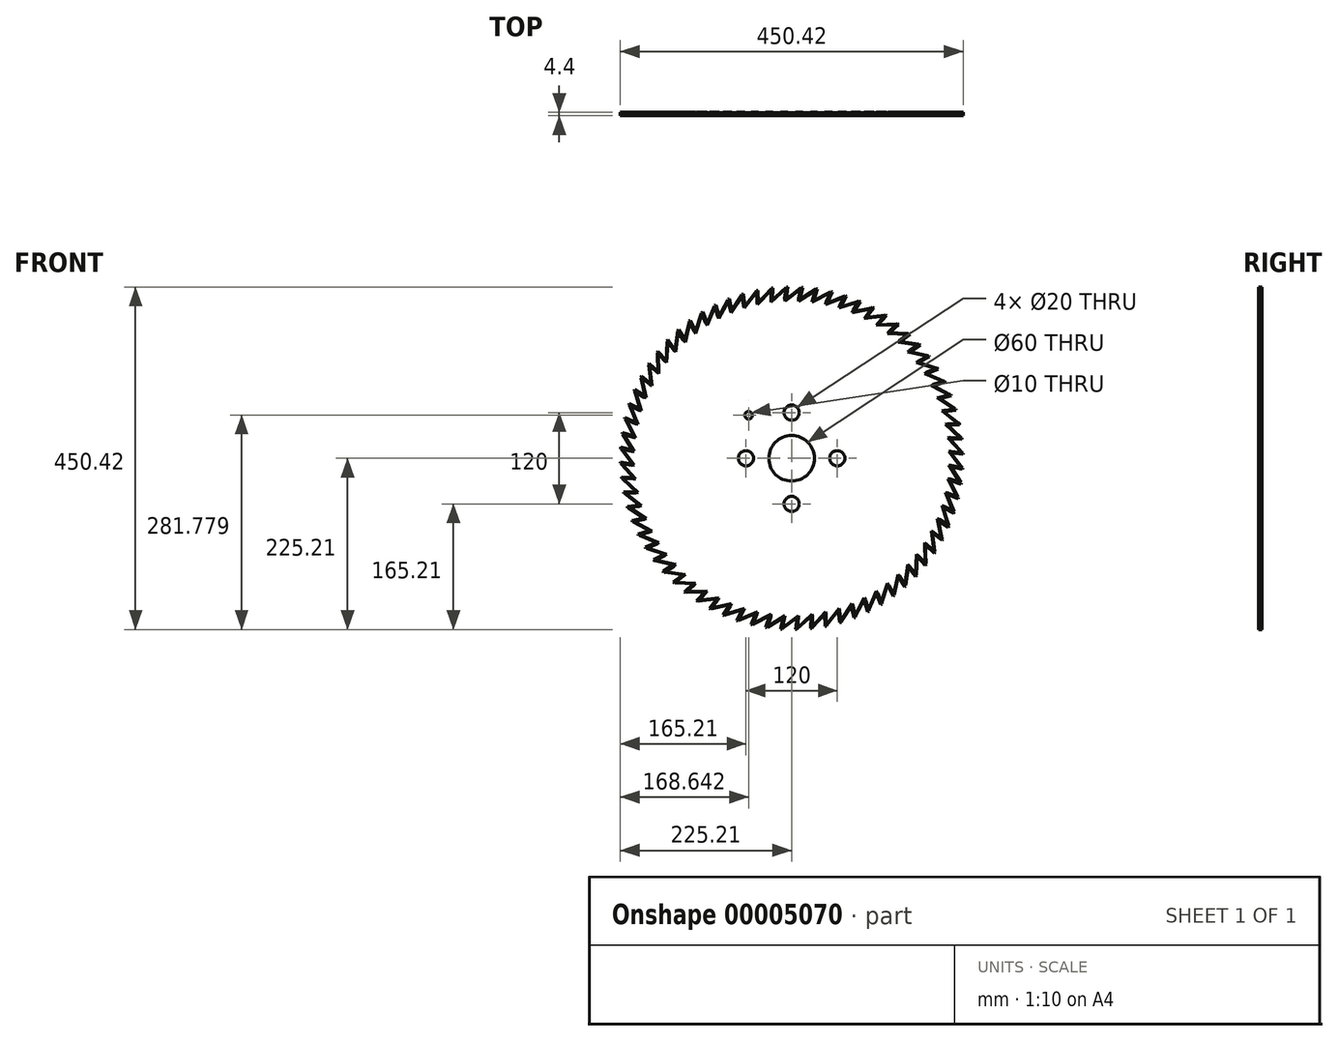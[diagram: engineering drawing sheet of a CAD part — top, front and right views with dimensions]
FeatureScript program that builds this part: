
annotation { "Feature Type Name" : "Feature", "Feature Type Description" : "" }
export const myFeature = defineFeature(function(context is Context, id is Id, definition is map)
    precondition{}
    {
        {
            var Q0;
            Q0=qCreatedBy(makeId("Right.planeOp"),FACE);
            var sketch = newSketch(context, id + "F0", { "sketchPlane" : qUnion([Q0])});
            skLineSegment(sketch, "E0", {"start": v(-63.93, 0) * mm, "end": v(105.28, 0) * mm, "construction": true});
            skSolve(sketch);
        }
        {
            var Q0;
            Q0=qCreatedBy(makeId("Front.planeOp"),FACE);
            var sketch = newSketch(context, id + "F1", { "sketchPlane" : qUnion([Q0])});
            skLineSegment(sketch, "E1", {"start": v(0, 0) * mm, "end": v(-1.3, 29.97) * mm, "construction": true});
            skLineSegment(sketch, "E2", {"start": v(-9.08, 208) * mm, "end": v(12.27, 224) * mm});
            skLineSegment(sketch, "E3", {"start": v(12.27, 224) * mm, "end": v(9.17, 210) * mm});
            skLineSegment(sketch, "E4", {"start": v(9.17, 210) * mm, "end": v(1.3, 29.97) * mm});
            skLineSegment(sketch, "E5", {"start": v(-1.3, 29.97) * mm, "end": v(-9.08, 208) * mm});
            skLineSegment(sketch, "E6", {"start": v(1.3, 29.97) * mm, "end": v(0, 0) * mm, "construction": true});
            skArc(sketch, "E7", {"start": v(1.3, 29.97) * mm, "mid": v(0, 30) * mm, "end": v(-1.3, 29.97) * mm});
            skArc(sketch, "E8", {"start": v(-1.3, 29.97) * mm, "mid": v(0, -30) * mm, "end": v(1.3, 29.97) * mm, "construction": true});
            skSolve(sketch);
        }
        {
            var Q0;
            Q0=qSketchRegion(id+"F1",true);
            extrude(context, id + "F2", {"entities" : qUnion([Q0]), "depth" : 4 * mm});
        }
        {
            var Q0;
            Q0=makeQuery(id+"F2.opExtrude","CAP_EDGE",EDGE,{"disambiguationData":[OSD([sQuery(id+"F1.wireOp",EDGE,"E2")])],"isStart":true});
            var Q1;
            Q1=makeQuery(id+"F2.opExtrude","CAP_EDGE",EDGE,{"disambiguationData":[OSD([sQuery(id+"F1.wireOp",EDGE,"E2")])],"isStart":false});
            chamfer(context, id + "F3", {"entities" : qUnion([Q0, Q1]), "width" : 1 * mm, "tangentPropagation" : true});
        }
        {
            var Q0;
            Q0=makeQuery(id+"F2.opExtrude","CAP_FACE",FACE,{"disambiguationData":[OSD([sQuery(id+"F1.wireOp",EDGE,"E2"),sQuery(id+"F1.wireOp",EDGE,"E3"),sQuery(id+"F1.wireOp",EDGE,"E4"),sQuery(id+"F1.wireOp",EDGE,"E5"),sQuery(id+"F1.wireOp",EDGE,"E7")])],"isStart":false});
            var Q1;
            Q1=makeQuery(id+"F2.opExtrude","SWEPT_FACE",FACE,{"disambiguationData":[OSD([sQuery(id+"F1.wireOp",EDGE,"E4")])]});
            var Q2;
            Q2=makeQuery(id+"F2.opExtrude","SWEPT_FACE",FACE,{"disambiguationData":[OSD([sQuery(id+"F1.wireOp",EDGE,"E3")])]});
            var Q3;
            Q3=makeQuery(id+"F2.opExtrude","SWEPT_FACE",FACE,{"disambiguationData":[OSD([sQuery(id+"F1.wireOp",EDGE,"E2")])]});
            var Q4;
            Q4=makeQuery(id+"F2.opExtrude","SWEPT_FACE",FACE,{"disambiguationData":[OSD([sQuery(id+"F1.wireOp",EDGE,"E5")])]});
            var Q5;
            Q5=makeQuery(id+"F2.opExtrude","CAP_FACE",FACE,{"disambiguationData":[OSD([sQuery(id+"F1.wireOp",EDGE,"E2"),sQuery(id+"F1.wireOp",EDGE,"E3"),sQuery(id+"F1.wireOp",EDGE,"E4"),sQuery(id+"F1.wireOp",EDGE,"E5"),sQuery(id+"F1.wireOp",EDGE,"E7")])],"isStart":true});
            var Q6;
            Q6=makeQuery(id+"F2.opExtrude","SWEPT_FACE",FACE,{"disambiguationData":[OSD([sQuery(id+"F1.wireOp",EDGE,"E7")])]});
            var Q7;
            {var subQ0=sQuery(id+"F1.wireOp",EDGE,"E2");Q7=makeQuery(id+"F3.opChamfer","BLEND_FACE",FACE,{"disambiguationData":[OSD([subQ0]),TDD([makeQuery(id+"F2.opExtrude","CAP_EDGE",EDGE,{"disambiguationData":[OSD([subQ0])],"isStart":false})])]});}
            var Q8;
            {var subQ0=sQuery(id+"F1.wireOp",EDGE,"E2");Q8=makeQuery(id+"F3.opChamfer","BLEND_FACE",FACE,{"disambiguationData":[OSD([subQ0]),TDD([makeQuery(id+"F2.opExtrude","CAP_EDGE",EDGE,{"disambiguationData":[OSD([subQ0])],"isStart":true})])]});}
            var Q9;
            Q9=makeQuery(id+"F2.opExtrude","SWEPT_BODY",BODY,{"disambiguationData":[OSD([sQuery(id+"F1.wireOp",EDGE,"E2"),sQuery(id+"F1.wireOp",EDGE,"E3"),sQuery(id+"F1.wireOp",EDGE,"E4"),sQuery(id+"F1.wireOp",EDGE,"E5"),sQuery(id+"F1.wireOp",EDGE,"E7")])]});
            var Q10;
            Q10=sQuery(id+"F0.wireOp",EDGE,"E0");
            circularPattern(context, id + "F4", {"faces" : qUnion([Q0, Q1, Q2, Q3, Q4, Q5, Q6, Q7, Q8]), "axis" : qUnion([Q10]), "angle" : 5 * degree, "instanceCount" : round(72), "patternType" : PatternType.FACE});
        }
        {
            var Q0;
            Q0=makeQuery(id+"F2.opExtrude","SWEPT_BODY",BODY,{"disambiguationData":[OSD([sQuery(id+"F1.wireOp",EDGE,"E2"),sQuery(id+"F1.wireOp",EDGE,"E3"),sQuery(id+"F1.wireOp",EDGE,"E4"),sQuery(id+"F1.wireOp",EDGE,"E5"),sQuery(id+"F1.wireOp",EDGE,"E7")])]});
            var Q1;
            Q1=makeQuery(id+"F4.opPattern","COPY",BODY,{"derivedFrom":makeQuery(id+"F2.opExtrude","SWEPT_BODY",BODY,{"disambiguationData":[OSD([sQuery(id+"F1.wireOp",EDGE,"E2"),sQuery(id+"F1.wireOp",EDGE,"E3"),sQuery(id+"F1.wireOp",EDGE,"E4"),sQuery(id+"F1.wireOp",EDGE,"E5"),sQuery(id+"F1.wireOp",EDGE,"E7")])]}),"instanceName":"1"});
            var Q2;
            Q2=makeQuery(id+"F4.opPattern","COPY",BODY,{"derivedFrom":makeQuery(id+"F2.opExtrude","SWEPT_BODY",BODY,{"disambiguationData":[OSD([sQuery(id+"F1.wireOp",EDGE,"E2"),sQuery(id+"F1.wireOp",EDGE,"E3"),sQuery(id+"F1.wireOp",EDGE,"E4"),sQuery(id+"F1.wireOp",EDGE,"E5"),sQuery(id+"F1.wireOp",EDGE,"E7")])]}),"instanceName":"2"});
            var Q3;
            Q3=makeQuery(id+"F4.opPattern","COPY",BODY,{"derivedFrom":makeQuery(id+"F2.opExtrude","SWEPT_BODY",BODY,{"disambiguationData":[OSD([sQuery(id+"F1.wireOp",EDGE,"E2"),sQuery(id+"F1.wireOp",EDGE,"E3"),sQuery(id+"F1.wireOp",EDGE,"E4"),sQuery(id+"F1.wireOp",EDGE,"E5"),sQuery(id+"F1.wireOp",EDGE,"E7")])]}),"instanceName":"3"});
            var Q4;
            Q4=makeQuery(id+"F4.opPattern","COPY",BODY,{"derivedFrom":makeQuery(id+"F2.opExtrude","SWEPT_BODY",BODY,{"disambiguationData":[OSD([sQuery(id+"F1.wireOp",EDGE,"E2"),sQuery(id+"F1.wireOp",EDGE,"E3"),sQuery(id+"F1.wireOp",EDGE,"E4"),sQuery(id+"F1.wireOp",EDGE,"E5"),sQuery(id+"F1.wireOp",EDGE,"E7")])]}),"instanceName":"4"});
            var Q5;
            Q5=makeQuery(id+"F4.opPattern","COPY",BODY,{"derivedFrom":makeQuery(id+"F2.opExtrude","SWEPT_BODY",BODY,{"disambiguationData":[OSD([sQuery(id+"F1.wireOp",EDGE,"E2"),sQuery(id+"F1.wireOp",EDGE,"E3"),sQuery(id+"F1.wireOp",EDGE,"E4"),sQuery(id+"F1.wireOp",EDGE,"E5"),sQuery(id+"F1.wireOp",EDGE,"E7")])]}),"instanceName":"5"});
            var Q6;
            Q6=makeQuery(id+"F4.opPattern","COPY",BODY,{"derivedFrom":makeQuery(id+"F2.opExtrude","SWEPT_BODY",BODY,{"disambiguationData":[OSD([sQuery(id+"F1.wireOp",EDGE,"E2"),sQuery(id+"F1.wireOp",EDGE,"E3"),sQuery(id+"F1.wireOp",EDGE,"E4"),sQuery(id+"F1.wireOp",EDGE,"E5"),sQuery(id+"F1.wireOp",EDGE,"E7")])]}),"instanceName":"6"});
            var Q7;
            Q7=makeQuery(id+"F4.opPattern","COPY",BODY,{"derivedFrom":makeQuery(id+"F2.opExtrude","SWEPT_BODY",BODY,{"disambiguationData":[OSD([sQuery(id+"F1.wireOp",EDGE,"E2"),sQuery(id+"F1.wireOp",EDGE,"E3"),sQuery(id+"F1.wireOp",EDGE,"E4"),sQuery(id+"F1.wireOp",EDGE,"E5"),sQuery(id+"F1.wireOp",EDGE,"E7")])]}),"instanceName":"7"});
            var Q8;
            Q8=makeQuery(id+"F4.opPattern","COPY",BODY,{"derivedFrom":makeQuery(id+"F2.opExtrude","SWEPT_BODY",BODY,{"disambiguationData":[OSD([sQuery(id+"F1.wireOp",EDGE,"E2"),sQuery(id+"F1.wireOp",EDGE,"E3"),sQuery(id+"F1.wireOp",EDGE,"E4"),sQuery(id+"F1.wireOp",EDGE,"E5"),sQuery(id+"F1.wireOp",EDGE,"E7")])]}),"instanceName":"8"});
            var Q9;
            Q9=makeQuery(id+"F4.opPattern","COPY",BODY,{"derivedFrom":makeQuery(id+"F2.opExtrude","SWEPT_BODY",BODY,{"disambiguationData":[OSD([sQuery(id+"F1.wireOp",EDGE,"E2"),sQuery(id+"F1.wireOp",EDGE,"E3"),sQuery(id+"F1.wireOp",EDGE,"E4"),sQuery(id+"F1.wireOp",EDGE,"E5"),sQuery(id+"F1.wireOp",EDGE,"E7")])]}),"instanceName":"9"});
            var Q10;
            Q10=makeQuery(id+"F4.opPattern","COPY",BODY,{"derivedFrom":makeQuery(id+"F2.opExtrude","SWEPT_BODY",BODY,{"disambiguationData":[OSD([sQuery(id+"F1.wireOp",EDGE,"E2"),sQuery(id+"F1.wireOp",EDGE,"E3"),sQuery(id+"F1.wireOp",EDGE,"E4"),sQuery(id+"F1.wireOp",EDGE,"E5"),sQuery(id+"F1.wireOp",EDGE,"E7")])]}),"instanceName":"10"});
            var Q11;
            Q11=makeQuery(id+"F4.opPattern","COPY",BODY,{"derivedFrom":makeQuery(id+"F2.opExtrude","SWEPT_BODY",BODY,{"disambiguationData":[OSD([sQuery(id+"F1.wireOp",EDGE,"E2"),sQuery(id+"F1.wireOp",EDGE,"E3"),sQuery(id+"F1.wireOp",EDGE,"E4"),sQuery(id+"F1.wireOp",EDGE,"E5"),sQuery(id+"F1.wireOp",EDGE,"E7")])]}),"instanceName":"11"});
            var Q12;
            Q12=makeQuery(id+"F4.opPattern","COPY",BODY,{"derivedFrom":makeQuery(id+"F2.opExtrude","SWEPT_BODY",BODY,{"disambiguationData":[OSD([sQuery(id+"F1.wireOp",EDGE,"E2"),sQuery(id+"F1.wireOp",EDGE,"E3"),sQuery(id+"F1.wireOp",EDGE,"E4"),sQuery(id+"F1.wireOp",EDGE,"E5"),sQuery(id+"F1.wireOp",EDGE,"E7")])]}),"instanceName":"12"});
            var Q13;
            Q13=makeQuery(id+"F4.opPattern","COPY",BODY,{"derivedFrom":makeQuery(id+"F2.opExtrude","SWEPT_BODY",BODY,{"disambiguationData":[OSD([sQuery(id+"F1.wireOp",EDGE,"E2"),sQuery(id+"F1.wireOp",EDGE,"E3"),sQuery(id+"F1.wireOp",EDGE,"E4"),sQuery(id+"F1.wireOp",EDGE,"E5"),sQuery(id+"F1.wireOp",EDGE,"E7")])]}),"instanceName":"13"});
            var Q14;
            Q14=makeQuery(id+"F4.opPattern","COPY",BODY,{"derivedFrom":makeQuery(id+"F2.opExtrude","SWEPT_BODY",BODY,{"disambiguationData":[OSD([sQuery(id+"F1.wireOp",EDGE,"E2"),sQuery(id+"F1.wireOp",EDGE,"E3"),sQuery(id+"F1.wireOp",EDGE,"E4"),sQuery(id+"F1.wireOp",EDGE,"E5"),sQuery(id+"F1.wireOp",EDGE,"E7")])]}),"instanceName":"14"});
            var Q15;
            Q15=makeQuery(id+"F4.opPattern","COPY",BODY,{"derivedFrom":makeQuery(id+"F2.opExtrude","SWEPT_BODY",BODY,{"disambiguationData":[OSD([sQuery(id+"F1.wireOp",EDGE,"E2"),sQuery(id+"F1.wireOp",EDGE,"E3"),sQuery(id+"F1.wireOp",EDGE,"E4"),sQuery(id+"F1.wireOp",EDGE,"E5"),sQuery(id+"F1.wireOp",EDGE,"E7")])]}),"instanceName":"15"});
            var Q16;
            Q16=makeQuery(id+"F4.opPattern","COPY",BODY,{"derivedFrom":makeQuery(id+"F2.opExtrude","SWEPT_BODY",BODY,{"disambiguationData":[OSD([sQuery(id+"F1.wireOp",EDGE,"E2"),sQuery(id+"F1.wireOp",EDGE,"E3"),sQuery(id+"F1.wireOp",EDGE,"E4"),sQuery(id+"F1.wireOp",EDGE,"E5"),sQuery(id+"F1.wireOp",EDGE,"E7")])]}),"instanceName":"16"});
            var Q17;
            Q17=makeQuery(id+"F4.opPattern","COPY",BODY,{"derivedFrom":makeQuery(id+"F2.opExtrude","SWEPT_BODY",BODY,{"disambiguationData":[OSD([sQuery(id+"F1.wireOp",EDGE,"E2"),sQuery(id+"F1.wireOp",EDGE,"E3"),sQuery(id+"F1.wireOp",EDGE,"E4"),sQuery(id+"F1.wireOp",EDGE,"E5"),sQuery(id+"F1.wireOp",EDGE,"E7")])]}),"instanceName":"17"});
            var Q18;
            Q18=makeQuery(id+"F4.opPattern","COPY",BODY,{"derivedFrom":makeQuery(id+"F2.opExtrude","SWEPT_BODY",BODY,{"disambiguationData":[OSD([sQuery(id+"F1.wireOp",EDGE,"E2"),sQuery(id+"F1.wireOp",EDGE,"E3"),sQuery(id+"F1.wireOp",EDGE,"E4"),sQuery(id+"F1.wireOp",EDGE,"E5"),sQuery(id+"F1.wireOp",EDGE,"E7")])]}),"instanceName":"18"});
            var Q19;
            Q19=makeQuery(id+"F4.opPattern","COPY",BODY,{"derivedFrom":makeQuery(id+"F2.opExtrude","SWEPT_BODY",BODY,{"disambiguationData":[OSD([sQuery(id+"F1.wireOp",EDGE,"E2"),sQuery(id+"F1.wireOp",EDGE,"E3"),sQuery(id+"F1.wireOp",EDGE,"E4"),sQuery(id+"F1.wireOp",EDGE,"E5"),sQuery(id+"F1.wireOp",EDGE,"E7")])]}),"instanceName":"19"});
            var Q20;
            Q20=makeQuery(id+"F4.opPattern","COPY",BODY,{"derivedFrom":makeQuery(id+"F2.opExtrude","SWEPT_BODY",BODY,{"disambiguationData":[OSD([sQuery(id+"F1.wireOp",EDGE,"E2"),sQuery(id+"F1.wireOp",EDGE,"E3"),sQuery(id+"F1.wireOp",EDGE,"E4"),sQuery(id+"F1.wireOp",EDGE,"E5"),sQuery(id+"F1.wireOp",EDGE,"E7")])]}),"instanceName":"20"});
            var Q21;
            Q21=makeQuery(id+"F4.opPattern","COPY",BODY,{"derivedFrom":makeQuery(id+"F2.opExtrude","SWEPT_BODY",BODY,{"disambiguationData":[OSD([sQuery(id+"F1.wireOp",EDGE,"E2"),sQuery(id+"F1.wireOp",EDGE,"E3"),sQuery(id+"F1.wireOp",EDGE,"E4"),sQuery(id+"F1.wireOp",EDGE,"E5"),sQuery(id+"F1.wireOp",EDGE,"E7")])]}),"instanceName":"21"});
            var Q22;
            Q22=makeQuery(id+"F4.opPattern","COPY",BODY,{"derivedFrom":makeQuery(id+"F2.opExtrude","SWEPT_BODY",BODY,{"disambiguationData":[OSD([sQuery(id+"F1.wireOp",EDGE,"E2"),sQuery(id+"F1.wireOp",EDGE,"E3"),sQuery(id+"F1.wireOp",EDGE,"E4"),sQuery(id+"F1.wireOp",EDGE,"E5"),sQuery(id+"F1.wireOp",EDGE,"E7")])]}),"instanceName":"22"});
            var Q23;
            Q23=makeQuery(id+"F4.opPattern","COPY",BODY,{"derivedFrom":makeQuery(id+"F2.opExtrude","SWEPT_BODY",BODY,{"disambiguationData":[OSD([sQuery(id+"F1.wireOp",EDGE,"E2"),sQuery(id+"F1.wireOp",EDGE,"E3"),sQuery(id+"F1.wireOp",EDGE,"E4"),sQuery(id+"F1.wireOp",EDGE,"E5"),sQuery(id+"F1.wireOp",EDGE,"E7")])]}),"instanceName":"23"});
            var Q24;
            Q24=makeQuery(id+"F4.opPattern","COPY",BODY,{"derivedFrom":makeQuery(id+"F2.opExtrude","SWEPT_BODY",BODY,{"disambiguationData":[OSD([sQuery(id+"F1.wireOp",EDGE,"E2"),sQuery(id+"F1.wireOp",EDGE,"E3"),sQuery(id+"F1.wireOp",EDGE,"E4"),sQuery(id+"F1.wireOp",EDGE,"E5"),sQuery(id+"F1.wireOp",EDGE,"E7")])]}),"instanceName":"24"});
            var Q25;
            Q25=makeQuery(id+"F4.opPattern","COPY",BODY,{"derivedFrom":makeQuery(id+"F2.opExtrude","SWEPT_BODY",BODY,{"disambiguationData":[OSD([sQuery(id+"F1.wireOp",EDGE,"E2"),sQuery(id+"F1.wireOp",EDGE,"E3"),sQuery(id+"F1.wireOp",EDGE,"E4"),sQuery(id+"F1.wireOp",EDGE,"E5"),sQuery(id+"F1.wireOp",EDGE,"E7")])]}),"instanceName":"25"});
            var Q26;
            Q26=makeQuery(id+"F4.opPattern","COPY",BODY,{"derivedFrom":makeQuery(id+"F2.opExtrude","SWEPT_BODY",BODY,{"disambiguationData":[OSD([sQuery(id+"F1.wireOp",EDGE,"E2"),sQuery(id+"F1.wireOp",EDGE,"E3"),sQuery(id+"F1.wireOp",EDGE,"E4"),sQuery(id+"F1.wireOp",EDGE,"E5"),sQuery(id+"F1.wireOp",EDGE,"E7")])]}),"instanceName":"26"});
            var Q27;
            Q27=makeQuery(id+"F4.opPattern","COPY",BODY,{"derivedFrom":makeQuery(id+"F2.opExtrude","SWEPT_BODY",BODY,{"disambiguationData":[OSD([sQuery(id+"F1.wireOp",EDGE,"E2"),sQuery(id+"F1.wireOp",EDGE,"E3"),sQuery(id+"F1.wireOp",EDGE,"E4"),sQuery(id+"F1.wireOp",EDGE,"E5"),sQuery(id+"F1.wireOp",EDGE,"E7")])]}),"instanceName":"27"});
            var Q28;
            Q28=makeQuery(id+"F4.opPattern","COPY",BODY,{"derivedFrom":makeQuery(id+"F2.opExtrude","SWEPT_BODY",BODY,{"disambiguationData":[OSD([sQuery(id+"F1.wireOp",EDGE,"E2"),sQuery(id+"F1.wireOp",EDGE,"E3"),sQuery(id+"F1.wireOp",EDGE,"E4"),sQuery(id+"F1.wireOp",EDGE,"E5"),sQuery(id+"F1.wireOp",EDGE,"E7")])]}),"instanceName":"28"});
            var Q29;
            Q29=makeQuery(id+"F4.opPattern","COPY",BODY,{"derivedFrom":makeQuery(id+"F2.opExtrude","SWEPT_BODY",BODY,{"disambiguationData":[OSD([sQuery(id+"F1.wireOp",EDGE,"E2"),sQuery(id+"F1.wireOp",EDGE,"E3"),sQuery(id+"F1.wireOp",EDGE,"E4"),sQuery(id+"F1.wireOp",EDGE,"E5"),sQuery(id+"F1.wireOp",EDGE,"E7")])]}),"instanceName":"29"});
            var Q30;
            Q30=makeQuery(id+"F4.opPattern","COPY",BODY,{"derivedFrom":makeQuery(id+"F2.opExtrude","SWEPT_BODY",BODY,{"disambiguationData":[OSD([sQuery(id+"F1.wireOp",EDGE,"E2"),sQuery(id+"F1.wireOp",EDGE,"E3"),sQuery(id+"F1.wireOp",EDGE,"E4"),sQuery(id+"F1.wireOp",EDGE,"E5"),sQuery(id+"F1.wireOp",EDGE,"E7")])]}),"instanceName":"30"});
            var Q31;
            Q31=makeQuery(id+"F4.opPattern","COPY",BODY,{"derivedFrom":makeQuery(id+"F2.opExtrude","SWEPT_BODY",BODY,{"disambiguationData":[OSD([sQuery(id+"F1.wireOp",EDGE,"E2"),sQuery(id+"F1.wireOp",EDGE,"E3"),sQuery(id+"F1.wireOp",EDGE,"E4"),sQuery(id+"F1.wireOp",EDGE,"E5"),sQuery(id+"F1.wireOp",EDGE,"E7")])]}),"instanceName":"31"});
            var Q32;
            Q32=makeQuery(id+"F4.opPattern","COPY",BODY,{"derivedFrom":makeQuery(id+"F2.opExtrude","SWEPT_BODY",BODY,{"disambiguationData":[OSD([sQuery(id+"F1.wireOp",EDGE,"E2"),sQuery(id+"F1.wireOp",EDGE,"E3"),sQuery(id+"F1.wireOp",EDGE,"E4"),sQuery(id+"F1.wireOp",EDGE,"E5"),sQuery(id+"F1.wireOp",EDGE,"E7")])]}),"instanceName":"32"});
            var Q33;
            Q33=makeQuery(id+"F4.opPattern","COPY",BODY,{"derivedFrom":makeQuery(id+"F2.opExtrude","SWEPT_BODY",BODY,{"disambiguationData":[OSD([sQuery(id+"F1.wireOp",EDGE,"E2"),sQuery(id+"F1.wireOp",EDGE,"E3"),sQuery(id+"F1.wireOp",EDGE,"E4"),sQuery(id+"F1.wireOp",EDGE,"E5"),sQuery(id+"F1.wireOp",EDGE,"E7")])]}),"instanceName":"33"});
            var Q34;
            Q34=makeQuery(id+"F4.opPattern","COPY",BODY,{"derivedFrom":makeQuery(id+"F2.opExtrude","SWEPT_BODY",BODY,{"disambiguationData":[OSD([sQuery(id+"F1.wireOp",EDGE,"E2"),sQuery(id+"F1.wireOp",EDGE,"E3"),sQuery(id+"F1.wireOp",EDGE,"E4"),sQuery(id+"F1.wireOp",EDGE,"E5"),sQuery(id+"F1.wireOp",EDGE,"E7")])]}),"instanceName":"34"});
            var Q35;
            Q35=makeQuery(id+"F4.opPattern","COPY",BODY,{"derivedFrom":makeQuery(id+"F2.opExtrude","SWEPT_BODY",BODY,{"disambiguationData":[OSD([sQuery(id+"F1.wireOp",EDGE,"E2"),sQuery(id+"F1.wireOp",EDGE,"E3"),sQuery(id+"F1.wireOp",EDGE,"E4"),sQuery(id+"F1.wireOp",EDGE,"E5"),sQuery(id+"F1.wireOp",EDGE,"E7")])]}),"instanceName":"35"});
            var Q36;
            Q36=makeQuery(id+"F4.opPattern","COPY",BODY,{"derivedFrom":makeQuery(id+"F2.opExtrude","SWEPT_BODY",BODY,{"disambiguationData":[OSD([sQuery(id+"F1.wireOp",EDGE,"E2"),sQuery(id+"F1.wireOp",EDGE,"E3"),sQuery(id+"F1.wireOp",EDGE,"E4"),sQuery(id+"F1.wireOp",EDGE,"E5"),sQuery(id+"F1.wireOp",EDGE,"E7")])]}),"instanceName":"36"});
            var Q37;
            Q37=makeQuery(id+"F4.opPattern","COPY",BODY,{"derivedFrom":makeQuery(id+"F2.opExtrude","SWEPT_BODY",BODY,{"disambiguationData":[OSD([sQuery(id+"F1.wireOp",EDGE,"E2"),sQuery(id+"F1.wireOp",EDGE,"E3"),sQuery(id+"F1.wireOp",EDGE,"E4"),sQuery(id+"F1.wireOp",EDGE,"E5"),sQuery(id+"F1.wireOp",EDGE,"E7")])]}),"instanceName":"37"});
            var Q38;
            Q38=makeQuery(id+"F4.opPattern","COPY",BODY,{"derivedFrom":makeQuery(id+"F2.opExtrude","SWEPT_BODY",BODY,{"disambiguationData":[OSD([sQuery(id+"F1.wireOp",EDGE,"E2"),sQuery(id+"F1.wireOp",EDGE,"E3"),sQuery(id+"F1.wireOp",EDGE,"E4"),sQuery(id+"F1.wireOp",EDGE,"E5"),sQuery(id+"F1.wireOp",EDGE,"E7")])]}),"instanceName":"38"});
            var Q39;
            Q39=makeQuery(id+"F4.opPattern","COPY",BODY,{"derivedFrom":makeQuery(id+"F2.opExtrude","SWEPT_BODY",BODY,{"disambiguationData":[OSD([sQuery(id+"F1.wireOp",EDGE,"E2"),sQuery(id+"F1.wireOp",EDGE,"E3"),sQuery(id+"F1.wireOp",EDGE,"E4"),sQuery(id+"F1.wireOp",EDGE,"E5"),sQuery(id+"F1.wireOp",EDGE,"E7")])]}),"instanceName":"39"});
            var Q40;
            Q40=makeQuery(id+"F4.opPattern","COPY",BODY,{"derivedFrom":makeQuery(id+"F2.opExtrude","SWEPT_BODY",BODY,{"disambiguationData":[OSD([sQuery(id+"F1.wireOp",EDGE,"E2"),sQuery(id+"F1.wireOp",EDGE,"E3"),sQuery(id+"F1.wireOp",EDGE,"E4"),sQuery(id+"F1.wireOp",EDGE,"E5"),sQuery(id+"F1.wireOp",EDGE,"E7")])]}),"instanceName":"40"});
            var Q41;
            Q41=makeQuery(id+"F4.opPattern","COPY",BODY,{"derivedFrom":makeQuery(id+"F2.opExtrude","SWEPT_BODY",BODY,{"disambiguationData":[OSD([sQuery(id+"F1.wireOp",EDGE,"E2"),sQuery(id+"F1.wireOp",EDGE,"E3"),sQuery(id+"F1.wireOp",EDGE,"E4"),sQuery(id+"F1.wireOp",EDGE,"E5"),sQuery(id+"F1.wireOp",EDGE,"E7")])]}),"instanceName":"41"});
            var Q42;
            Q42=makeQuery(id+"F4.opPattern","COPY",BODY,{"derivedFrom":makeQuery(id+"F2.opExtrude","SWEPT_BODY",BODY,{"disambiguationData":[OSD([sQuery(id+"F1.wireOp",EDGE,"E2"),sQuery(id+"F1.wireOp",EDGE,"E3"),sQuery(id+"F1.wireOp",EDGE,"E4"),sQuery(id+"F1.wireOp",EDGE,"E5"),sQuery(id+"F1.wireOp",EDGE,"E7")])]}),"instanceName":"42"});
            var Q43;
            Q43=makeQuery(id+"F4.opPattern","COPY",BODY,{"derivedFrom":makeQuery(id+"F2.opExtrude","SWEPT_BODY",BODY,{"disambiguationData":[OSD([sQuery(id+"F1.wireOp",EDGE,"E2"),sQuery(id+"F1.wireOp",EDGE,"E3"),sQuery(id+"F1.wireOp",EDGE,"E4"),sQuery(id+"F1.wireOp",EDGE,"E5"),sQuery(id+"F1.wireOp",EDGE,"E7")])]}),"instanceName":"43"});
            var Q44;
            Q44=makeQuery(id+"F4.opPattern","COPY",BODY,{"derivedFrom":makeQuery(id+"F2.opExtrude","SWEPT_BODY",BODY,{"disambiguationData":[OSD([sQuery(id+"F1.wireOp",EDGE,"E2"),sQuery(id+"F1.wireOp",EDGE,"E3"),sQuery(id+"F1.wireOp",EDGE,"E4"),sQuery(id+"F1.wireOp",EDGE,"E5"),sQuery(id+"F1.wireOp",EDGE,"E7")])]}),"instanceName":"44"});
            var Q45;
            Q45=makeQuery(id+"F4.opPattern","COPY",BODY,{"derivedFrom":makeQuery(id+"F2.opExtrude","SWEPT_BODY",BODY,{"disambiguationData":[OSD([sQuery(id+"F1.wireOp",EDGE,"E2"),sQuery(id+"F1.wireOp",EDGE,"E3"),sQuery(id+"F1.wireOp",EDGE,"E4"),sQuery(id+"F1.wireOp",EDGE,"E5"),sQuery(id+"F1.wireOp",EDGE,"E7")])]}),"instanceName":"45"});
            var Q46;
            Q46=makeQuery(id+"F4.opPattern","COPY",BODY,{"derivedFrom":makeQuery(id+"F2.opExtrude","SWEPT_BODY",BODY,{"disambiguationData":[OSD([sQuery(id+"F1.wireOp",EDGE,"E2"),sQuery(id+"F1.wireOp",EDGE,"E3"),sQuery(id+"F1.wireOp",EDGE,"E4"),sQuery(id+"F1.wireOp",EDGE,"E5"),sQuery(id+"F1.wireOp",EDGE,"E7")])]}),"instanceName":"46"});
            var Q47;
            Q47=makeQuery(id+"F4.opPattern","COPY",BODY,{"derivedFrom":makeQuery(id+"F2.opExtrude","SWEPT_BODY",BODY,{"disambiguationData":[OSD([sQuery(id+"F1.wireOp",EDGE,"E2"),sQuery(id+"F1.wireOp",EDGE,"E3"),sQuery(id+"F1.wireOp",EDGE,"E4"),sQuery(id+"F1.wireOp",EDGE,"E5"),sQuery(id+"F1.wireOp",EDGE,"E7")])]}),"instanceName":"47"});
            var Q48;
            Q48=makeQuery(id+"F4.opPattern","COPY",BODY,{"derivedFrom":makeQuery(id+"F2.opExtrude","SWEPT_BODY",BODY,{"disambiguationData":[OSD([sQuery(id+"F1.wireOp",EDGE,"E2"),sQuery(id+"F1.wireOp",EDGE,"E3"),sQuery(id+"F1.wireOp",EDGE,"E4"),sQuery(id+"F1.wireOp",EDGE,"E5"),sQuery(id+"F1.wireOp",EDGE,"E7")])]}),"instanceName":"48"});
            var Q49;
            Q49=makeQuery(id+"F4.opPattern","COPY",BODY,{"derivedFrom":makeQuery(id+"F2.opExtrude","SWEPT_BODY",BODY,{"disambiguationData":[OSD([sQuery(id+"F1.wireOp",EDGE,"E2"),sQuery(id+"F1.wireOp",EDGE,"E3"),sQuery(id+"F1.wireOp",EDGE,"E4"),sQuery(id+"F1.wireOp",EDGE,"E5"),sQuery(id+"F1.wireOp",EDGE,"E7")])]}),"instanceName":"49"});
            var Q50;
            Q50=makeQuery(id+"F4.opPattern","COPY",BODY,{"derivedFrom":makeQuery(id+"F2.opExtrude","SWEPT_BODY",BODY,{"disambiguationData":[OSD([sQuery(id+"F1.wireOp",EDGE,"E2"),sQuery(id+"F1.wireOp",EDGE,"E3"),sQuery(id+"F1.wireOp",EDGE,"E4"),sQuery(id+"F1.wireOp",EDGE,"E5"),sQuery(id+"F1.wireOp",EDGE,"E7")])]}),"instanceName":"50"});
            var Q51;
            Q51=makeQuery(id+"F4.opPattern","COPY",BODY,{"derivedFrom":makeQuery(id+"F2.opExtrude","SWEPT_BODY",BODY,{"disambiguationData":[OSD([sQuery(id+"F1.wireOp",EDGE,"E2"),sQuery(id+"F1.wireOp",EDGE,"E3"),sQuery(id+"F1.wireOp",EDGE,"E4"),sQuery(id+"F1.wireOp",EDGE,"E5"),sQuery(id+"F1.wireOp",EDGE,"E7")])]}),"instanceName":"51"});
            var Q52;
            Q52=makeQuery(id+"F4.opPattern","COPY",BODY,{"derivedFrom":makeQuery(id+"F2.opExtrude","SWEPT_BODY",BODY,{"disambiguationData":[OSD([sQuery(id+"F1.wireOp",EDGE,"E2"),sQuery(id+"F1.wireOp",EDGE,"E3"),sQuery(id+"F1.wireOp",EDGE,"E4"),sQuery(id+"F1.wireOp",EDGE,"E5"),sQuery(id+"F1.wireOp",EDGE,"E7")])]}),"instanceName":"52"});
            var Q53;
            Q53=makeQuery(id+"F4.opPattern","COPY",BODY,{"derivedFrom":makeQuery(id+"F2.opExtrude","SWEPT_BODY",BODY,{"disambiguationData":[OSD([sQuery(id+"F1.wireOp",EDGE,"E2"),sQuery(id+"F1.wireOp",EDGE,"E3"),sQuery(id+"F1.wireOp",EDGE,"E4"),sQuery(id+"F1.wireOp",EDGE,"E5"),sQuery(id+"F1.wireOp",EDGE,"E7")])]}),"instanceName":"53"});
            var Q54;
            Q54=makeQuery(id+"F4.opPattern","COPY",BODY,{"derivedFrom":makeQuery(id+"F2.opExtrude","SWEPT_BODY",BODY,{"disambiguationData":[OSD([sQuery(id+"F1.wireOp",EDGE,"E2"),sQuery(id+"F1.wireOp",EDGE,"E3"),sQuery(id+"F1.wireOp",EDGE,"E4"),sQuery(id+"F1.wireOp",EDGE,"E5"),sQuery(id+"F1.wireOp",EDGE,"E7")])]}),"instanceName":"54"});
            var Q55;
            Q55=makeQuery(id+"F4.opPattern","COPY",BODY,{"derivedFrom":makeQuery(id+"F2.opExtrude","SWEPT_BODY",BODY,{"disambiguationData":[OSD([sQuery(id+"F1.wireOp",EDGE,"E2"),sQuery(id+"F1.wireOp",EDGE,"E3"),sQuery(id+"F1.wireOp",EDGE,"E4"),sQuery(id+"F1.wireOp",EDGE,"E5"),sQuery(id+"F1.wireOp",EDGE,"E7")])]}),"instanceName":"55"});
            var Q56;
            Q56=makeQuery(id+"F4.opPattern","COPY",BODY,{"derivedFrom":makeQuery(id+"F2.opExtrude","SWEPT_BODY",BODY,{"disambiguationData":[OSD([sQuery(id+"F1.wireOp",EDGE,"E2"),sQuery(id+"F1.wireOp",EDGE,"E3"),sQuery(id+"F1.wireOp",EDGE,"E4"),sQuery(id+"F1.wireOp",EDGE,"E5"),sQuery(id+"F1.wireOp",EDGE,"E7")])]}),"instanceName":"56"});
            var Q57;
            Q57=makeQuery(id+"F4.opPattern","COPY",BODY,{"derivedFrom":makeQuery(id+"F2.opExtrude","SWEPT_BODY",BODY,{"disambiguationData":[OSD([sQuery(id+"F1.wireOp",EDGE,"E2"),sQuery(id+"F1.wireOp",EDGE,"E3"),sQuery(id+"F1.wireOp",EDGE,"E4"),sQuery(id+"F1.wireOp",EDGE,"E5"),sQuery(id+"F1.wireOp",EDGE,"E7")])]}),"instanceName":"57"});
            var Q58;
            Q58=makeQuery(id+"F4.opPattern","COPY",BODY,{"derivedFrom":makeQuery(id+"F2.opExtrude","SWEPT_BODY",BODY,{"disambiguationData":[OSD([sQuery(id+"F1.wireOp",EDGE,"E2"),sQuery(id+"F1.wireOp",EDGE,"E3"),sQuery(id+"F1.wireOp",EDGE,"E4"),sQuery(id+"F1.wireOp",EDGE,"E5"),sQuery(id+"F1.wireOp",EDGE,"E7")])]}),"instanceName":"58"});
            var Q59;
            Q59=makeQuery(id+"F4.opPattern","COPY",BODY,{"derivedFrom":makeQuery(id+"F2.opExtrude","SWEPT_BODY",BODY,{"disambiguationData":[OSD([sQuery(id+"F1.wireOp",EDGE,"E2"),sQuery(id+"F1.wireOp",EDGE,"E3"),sQuery(id+"F1.wireOp",EDGE,"E4"),sQuery(id+"F1.wireOp",EDGE,"E5"),sQuery(id+"F1.wireOp",EDGE,"E7")])]}),"instanceName":"59"});
            var Q60;
            Q60=makeQuery(id+"F4.opPattern","COPY",BODY,{"derivedFrom":makeQuery(id+"F2.opExtrude","SWEPT_BODY",BODY,{"disambiguationData":[OSD([sQuery(id+"F1.wireOp",EDGE,"E2"),sQuery(id+"F1.wireOp",EDGE,"E3"),sQuery(id+"F1.wireOp",EDGE,"E4"),sQuery(id+"F1.wireOp",EDGE,"E5"),sQuery(id+"F1.wireOp",EDGE,"E7")])]}),"instanceName":"60"});
            var Q61;
            Q61=makeQuery(id+"F4.opPattern","COPY",BODY,{"derivedFrom":makeQuery(id+"F2.opExtrude","SWEPT_BODY",BODY,{"disambiguationData":[OSD([sQuery(id+"F1.wireOp",EDGE,"E2"),sQuery(id+"F1.wireOp",EDGE,"E3"),sQuery(id+"F1.wireOp",EDGE,"E4"),sQuery(id+"F1.wireOp",EDGE,"E5"),sQuery(id+"F1.wireOp",EDGE,"E7")])]}),"instanceName":"61"});
            var Q62;
            Q62=makeQuery(id+"F4.opPattern","COPY",BODY,{"derivedFrom":makeQuery(id+"F2.opExtrude","SWEPT_BODY",BODY,{"disambiguationData":[OSD([sQuery(id+"F1.wireOp",EDGE,"E2"),sQuery(id+"F1.wireOp",EDGE,"E3"),sQuery(id+"F1.wireOp",EDGE,"E4"),sQuery(id+"F1.wireOp",EDGE,"E5"),sQuery(id+"F1.wireOp",EDGE,"E7")])]}),"instanceName":"62"});
            var Q63;
            Q63=makeQuery(id+"F4.opPattern","COPY",BODY,{"derivedFrom":makeQuery(id+"F2.opExtrude","SWEPT_BODY",BODY,{"disambiguationData":[OSD([sQuery(id+"F1.wireOp",EDGE,"E2"),sQuery(id+"F1.wireOp",EDGE,"E3"),sQuery(id+"F1.wireOp",EDGE,"E4"),sQuery(id+"F1.wireOp",EDGE,"E5"),sQuery(id+"F1.wireOp",EDGE,"E7")])]}),"instanceName":"63"});
            var Q64;
            Q64=makeQuery(id+"F4.opPattern","COPY",BODY,{"derivedFrom":makeQuery(id+"F2.opExtrude","SWEPT_BODY",BODY,{"disambiguationData":[OSD([sQuery(id+"F1.wireOp",EDGE,"E2"),sQuery(id+"F1.wireOp",EDGE,"E3"),sQuery(id+"F1.wireOp",EDGE,"E4"),sQuery(id+"F1.wireOp",EDGE,"E5"),sQuery(id+"F1.wireOp",EDGE,"E7")])]}),"instanceName":"64"});
            var Q65;
            Q65=makeQuery(id+"F4.opPattern","COPY",BODY,{"derivedFrom":makeQuery(id+"F2.opExtrude","SWEPT_BODY",BODY,{"disambiguationData":[OSD([sQuery(id+"F1.wireOp",EDGE,"E2"),sQuery(id+"F1.wireOp",EDGE,"E3"),sQuery(id+"F1.wireOp",EDGE,"E4"),sQuery(id+"F1.wireOp",EDGE,"E5"),sQuery(id+"F1.wireOp",EDGE,"E7")])]}),"instanceName":"65"});
            var Q66;
            Q66=makeQuery(id+"F4.opPattern","COPY",BODY,{"derivedFrom":makeQuery(id+"F2.opExtrude","SWEPT_BODY",BODY,{"disambiguationData":[OSD([sQuery(id+"F1.wireOp",EDGE,"E2"),sQuery(id+"F1.wireOp",EDGE,"E3"),sQuery(id+"F1.wireOp",EDGE,"E4"),sQuery(id+"F1.wireOp",EDGE,"E5"),sQuery(id+"F1.wireOp",EDGE,"E7")])]}),"instanceName":"66"});
            var Q67;
            Q67=makeQuery(id+"F4.opPattern","COPY",BODY,{"derivedFrom":makeQuery(id+"F2.opExtrude","SWEPT_BODY",BODY,{"disambiguationData":[OSD([sQuery(id+"F1.wireOp",EDGE,"E2"),sQuery(id+"F1.wireOp",EDGE,"E3"),sQuery(id+"F1.wireOp",EDGE,"E4"),sQuery(id+"F1.wireOp",EDGE,"E5"),sQuery(id+"F1.wireOp",EDGE,"E7")])]}),"instanceName":"67"});
            var Q68;
            Q68=makeQuery(id+"F4.opPattern","COPY",BODY,{"derivedFrom":makeQuery(id+"F2.opExtrude","SWEPT_BODY",BODY,{"disambiguationData":[OSD([sQuery(id+"F1.wireOp",EDGE,"E2"),sQuery(id+"F1.wireOp",EDGE,"E3"),sQuery(id+"F1.wireOp",EDGE,"E4"),sQuery(id+"F1.wireOp",EDGE,"E5"),sQuery(id+"F1.wireOp",EDGE,"E7")])]}),"instanceName":"68"});
            var Q69;
            Q69=makeQuery(id+"F4.opPattern","COPY",BODY,{"derivedFrom":makeQuery(id+"F2.opExtrude","SWEPT_BODY",BODY,{"disambiguationData":[OSD([sQuery(id+"F1.wireOp",EDGE,"E2"),sQuery(id+"F1.wireOp",EDGE,"E3"),sQuery(id+"F1.wireOp",EDGE,"E4"),sQuery(id+"F1.wireOp",EDGE,"E5"),sQuery(id+"F1.wireOp",EDGE,"E7")])]}),"instanceName":"69"});
            var Q70;
            Q70=makeQuery(id+"F4.opPattern","COPY",BODY,{"derivedFrom":makeQuery(id+"F2.opExtrude","SWEPT_BODY",BODY,{"disambiguationData":[OSD([sQuery(id+"F1.wireOp",EDGE,"E2"),sQuery(id+"F1.wireOp",EDGE,"E3"),sQuery(id+"F1.wireOp",EDGE,"E4"),sQuery(id+"F1.wireOp",EDGE,"E5"),sQuery(id+"F1.wireOp",EDGE,"E7")])]}),"instanceName":"70"});
            var Q71;
            Q71=makeQuery(id+"F4.opPattern","COPY",BODY,{"derivedFrom":makeQuery(id+"F2.opExtrude","SWEPT_BODY",BODY,{"disambiguationData":[OSD([sQuery(id+"F1.wireOp",EDGE,"E2"),sQuery(id+"F1.wireOp",EDGE,"E3"),sQuery(id+"F1.wireOp",EDGE,"E4"),sQuery(id+"F1.wireOp",EDGE,"E5"),sQuery(id+"F1.wireOp",EDGE,"E7")])]}),"instanceName":"71"});
            booleanBodies(context, id + "F5", {"operationType" : BooleanOperationType.UNION, "tools" : qUnion([Q0, Q1, Q2, Q3, Q4, Q5, Q6, Q7, Q8, Q9, Q10, Q11, Q12, Q13, Q14, Q15, Q16, Q17, Q18, Q19, Q20, Q21, Q22, Q23, Q24, Q25, Q26, Q27, Q28, Q29, Q30, Q31, Q32, Q33, Q34, Q35, Q36, Q37, Q38, Q39, Q40, Q41, Q42, Q43, Q44, Q45, Q46, Q47, Q48, Q49, Q50, Q51, Q52, Q53, Q54, Q55, Q56, Q57, Q58, Q59, Q60, Q61, Q62, Q63, Q64, Q65, Q66, Q67, Q68, Q69, Q70, Q71])});
        }
        {
            var Q0;
            Q0=makeQuery(id+"F2.opExtrude","SWEPT_FACE",FACE,{"disambiguationData":[OSD([sQuery(id+"F1.wireOp",EDGE,"E3")])]});
            cPlane(context, id + "F6", {"entities" : qUnion([Q0]), "cplaneType" : CPlaneType.OFFSET, "offset" : 0 * mm, "width" : 150 * mm, "height" : 150 * mm});
        }
        {
            var Q0;
            Q0=qCreatedBy(id+"F6.planeOp",FACE);
            var sketch = newSketch(context, id + "F7", { "sketchPlane" : qUnion([Q0])});
            skLineSegment(sketch, "E9.bottom", {"start": v(-4.2, 222.35) * mm, "end": v(0.2, 222.35) * mm});
            skLineSegment(sketch, "E9.top", {"start": v(-4.2, 207) * mm, "end": v(0.2, 207) * mm});
            skLineSegment(sketch, "E9.left", {"start": v(-4.2, 222.35) * mm, "end": v(-4.2, 207) * mm});
            skLineSegment(sketch, "E9.right", {"start": v(0.2, 222.35) * mm, "end": v(0.2, 207) * mm});
            skSolve(sketch);
        }
        {
            var Q0;
            Q0=qSketchRegion(id+"F7",true);
            extrude(context, id + "F8", {"entities" : qUnion([Q0]), "depth" : 2 * mm});
        }
        {
            var Q0;
            Q0=makeQuery(id+"F8.opExtrude","SWEPT_BODY",BODY,{"disambiguationData":[OSD([sQuery(id+"F7.wireOp",EDGE,"E9.bottom"),sQuery(id+"F7.wireOp",EDGE,"E9.top"),sQuery(id+"F7.wireOp",EDGE,"E9.left"),sQuery(id+"F7.wireOp",EDGE,"E9.right")])]});
            var Q1;
            Q1=sQuery(id+"F0.wireOp",EDGE,"E0");
            circularPattern(context, id + "F9", {"entities" : qUnion([Q0]), "axis" : qUnion([Q1]), "angle" : 5 * degree, "instanceCount" : round(72)});
        }
        {
            var Q0;
            {var subQ0=makeQuery(id+"F2.opExtrude","CAP_FACE",FACE,{"disambiguationData":[OSD([sQuery(id+"F1.wireOp",EDGE,"E2"),sQuery(id+"F1.wireOp",EDGE,"E3"),sQuery(id+"F1.wireOp",EDGE,"E4"),sQuery(id+"F1.wireOp",EDGE,"E5"),sQuery(id+"F1.wireOp",EDGE,"E7")])],"isStart":false});Q0=makeQuery(id+"F5.opBoolean","MERGE",FACE,{"derivedFrom":[subQ0,makeQuery(id+"F4.opPattern","COPY",FACE,{"derivedFrom":subQ0,"instanceName":"1"}),makeQuery(id+"F4.opPattern","COPY",FACE,{"derivedFrom":subQ0,"instanceName":"2"}),makeQuery(id+"F4.opPattern","COPY",FACE,{"derivedFrom":subQ0,"instanceName":"3"}),makeQuery(id+"F4.opPattern","COPY",FACE,{"derivedFrom":subQ0,"instanceName":"4"}),makeQuery(id+"F4.opPattern","COPY",FACE,{"derivedFrom":subQ0,"instanceName":"5"}),makeQuery(id+"F4.opPattern","COPY",FACE,{"derivedFrom":subQ0,"instanceName":"6"}),makeQuery(id+"F4.opPattern","COPY",FACE,{"derivedFrom":subQ0,"instanceName":"7"}),makeQuery(id+"F4.opPattern","COPY",FACE,{"derivedFrom":subQ0,"instanceName":"8"}),makeQuery(id+"F4.opPattern","COPY",FACE,{"derivedFrom":subQ0,"instanceName":"9"}),makeQuery(id+"F4.opPattern","COPY",FACE,{"derivedFrom":subQ0,"instanceName":"10"}),makeQuery(id+"F4.opPattern","COPY",FACE,{"derivedFrom":subQ0,"instanceName":"11"}),makeQuery(id+"F4.opPattern","COPY",FACE,{"derivedFrom":subQ0,"instanceName":"12"}),makeQuery(id+"F4.opPattern","COPY",FACE,{"derivedFrom":subQ0,"instanceName":"13"}),makeQuery(id+"F4.opPattern","COPY",FACE,{"derivedFrom":subQ0,"instanceName":"14"}),makeQuery(id+"F4.opPattern","COPY",FACE,{"derivedFrom":subQ0,"instanceName":"15"}),makeQuery(id+"F4.opPattern","COPY",FACE,{"derivedFrom":subQ0,"instanceName":"16"}),makeQuery(id+"F4.opPattern","COPY",FACE,{"derivedFrom":subQ0,"instanceName":"17"}),makeQuery(id+"F4.opPattern","COPY",FACE,{"derivedFrom":subQ0,"instanceName":"18"}),makeQuery(id+"F4.opPattern","COPY",FACE,{"derivedFrom":subQ0,"instanceName":"19"}),makeQuery(id+"F4.opPattern","COPY",FACE,{"derivedFrom":subQ0,"instanceName":"20"}),makeQuery(id+"F4.opPattern","COPY",FACE,{"derivedFrom":subQ0,"instanceName":"21"}),makeQuery(id+"F4.opPattern","COPY",FACE,{"derivedFrom":subQ0,"instanceName":"22"}),makeQuery(id+"F4.opPattern","COPY",FACE,{"derivedFrom":subQ0,"instanceName":"23"}),makeQuery(id+"F4.opPattern","COPY",FACE,{"derivedFrom":subQ0,"instanceName":"24"}),makeQuery(id+"F4.opPattern","COPY",FACE,{"derivedFrom":subQ0,"instanceName":"25"}),makeQuery(id+"F4.opPattern","COPY",FACE,{"derivedFrom":subQ0,"instanceName":"26"}),makeQuery(id+"F4.opPattern","COPY",FACE,{"derivedFrom":subQ0,"instanceName":"27"}),makeQuery(id+"F4.opPattern","COPY",FACE,{"derivedFrom":subQ0,"instanceName":"28"}),makeQuery(id+"F4.opPattern","COPY",FACE,{"derivedFrom":subQ0,"instanceName":"29"}),makeQuery(id+"F4.opPattern","COPY",FACE,{"derivedFrom":subQ0,"instanceName":"30"}),makeQuery(id+"F4.opPattern","COPY",FACE,{"derivedFrom":subQ0,"instanceName":"31"}),makeQuery(id+"F4.opPattern","COPY",FACE,{"derivedFrom":subQ0,"instanceName":"32"}),makeQuery(id+"F4.opPattern","COPY",FACE,{"derivedFrom":subQ0,"instanceName":"33"}),makeQuery(id+"F4.opPattern","COPY",FACE,{"derivedFrom":subQ0,"instanceName":"34"}),makeQuery(id+"F4.opPattern","COPY",FACE,{"derivedFrom":subQ0,"instanceName":"35"}),makeQuery(id+"F4.opPattern","COPY",FACE,{"derivedFrom":subQ0,"instanceName":"36"}),makeQuery(id+"F4.opPattern","COPY",FACE,{"derivedFrom":subQ0,"instanceName":"37"}),makeQuery(id+"F4.opPattern","COPY",FACE,{"derivedFrom":subQ0,"instanceName":"38"}),makeQuery(id+"F4.opPattern","COPY",FACE,{"derivedFrom":subQ0,"instanceName":"39"}),makeQuery(id+"F4.opPattern","COPY",FACE,{"derivedFrom":subQ0,"instanceName":"40"}),makeQuery(id+"F4.opPattern","COPY",FACE,{"derivedFrom":subQ0,"instanceName":"41"}),makeQuery(id+"F4.opPattern","COPY",FACE,{"derivedFrom":subQ0,"instanceName":"42"}),makeQuery(id+"F4.opPattern","COPY",FACE,{"derivedFrom":subQ0,"instanceName":"43"}),makeQuery(id+"F4.opPattern","COPY",FACE,{"derivedFrom":subQ0,"instanceName":"44"}),makeQuery(id+"F4.opPattern","COPY",FACE,{"derivedFrom":subQ0,"instanceName":"45"}),makeQuery(id+"F4.opPattern","COPY",FACE,{"derivedFrom":subQ0,"instanceName":"46"}),makeQuery(id+"F4.opPattern","COPY",FACE,{"derivedFrom":subQ0,"instanceName":"47"}),makeQuery(id+"F4.opPattern","COPY",FACE,{"derivedFrom":subQ0,"instanceName":"48"}),makeQuery(id+"F4.opPattern","COPY",FACE,{"derivedFrom":subQ0,"instanceName":"49"}),makeQuery(id+"F4.opPattern","COPY",FACE,{"derivedFrom":subQ0,"instanceName":"50"}),makeQuery(id+"F4.opPattern","COPY",FACE,{"derivedFrom":subQ0,"instanceName":"51"}),makeQuery(id+"F4.opPattern","COPY",FACE,{"derivedFrom":subQ0,"instanceName":"52"}),makeQuery(id+"F4.opPattern","COPY",FACE,{"derivedFrom":subQ0,"instanceName":"53"}),makeQuery(id+"F4.opPattern","COPY",FACE,{"derivedFrom":subQ0,"instanceName":"54"}),makeQuery(id+"F4.opPattern","COPY",FACE,{"derivedFrom":subQ0,"instanceName":"55"}),makeQuery(id+"F4.opPattern","COPY",FACE,{"derivedFrom":subQ0,"instanceName":"56"}),makeQuery(id+"F4.opPattern","COPY",FACE,{"derivedFrom":subQ0,"instanceName":"57"}),makeQuery(id+"F4.opPattern","COPY",FACE,{"derivedFrom":subQ0,"instanceName":"58"}),makeQuery(id+"F4.opPattern","COPY",FACE,{"derivedFrom":subQ0,"instanceName":"59"}),makeQuery(id+"F4.opPattern","COPY",FACE,{"derivedFrom":subQ0,"instanceName":"60"}),makeQuery(id+"F4.opPattern","COPY",FACE,{"derivedFrom":subQ0,"instanceName":"61"}),makeQuery(id+"F4.opPattern","COPY",FACE,{"derivedFrom":subQ0,"instanceName":"62"}),makeQuery(id+"F4.opPattern","COPY",FACE,{"derivedFrom":subQ0,"instanceName":"63"}),makeQuery(id+"F4.opPattern","COPY",FACE,{"derivedFrom":subQ0,"instanceName":"64"}),makeQuery(id+"F4.opPattern","COPY",FACE,{"derivedFrom":subQ0,"instanceName":"65"}),makeQuery(id+"F4.opPattern","COPY",FACE,{"derivedFrom":subQ0,"instanceName":"66"}),makeQuery(id+"F4.opPattern","COPY",FACE,{"derivedFrom":subQ0,"instanceName":"67"}),makeQuery(id+"F4.opPattern","COPY",FACE,{"derivedFrom":subQ0,"instanceName":"68"}),makeQuery(id+"F4.opPattern","COPY",FACE,{"derivedFrom":subQ0,"instanceName":"69"}),makeQuery(id+"F4.opPattern","COPY",FACE,{"derivedFrom":subQ0,"instanceName":"70"}),makeQuery(id+"F4.opPattern","COPY",FACE,{"derivedFrom":subQ0,"instanceName":"71"})]});}
            var sketch = newSketch(context, id + "F10", { "sketchPlane" : qUnion([Q0])});
            skCircle(sketch, "E10", {"center": v(0, 60) * mm, "radius": 10 * mm});
            skSolve(sketch);
        }
        {
            var Q0;
            Q0=qSketchRegion(id+"F10",true);
            extrude(context, id + "F11", {"entities" : qUnion([Q0]), "operationType" : NewBodyOperationType.REMOVE, "endBound" : BoundingType.THROUGH_ALL, "oppositeDirection" : true, "depth" : 25 * mm});
        }
        {
            var Q0;
            Q0=makeQuery(id+"F11.boolean.opBoolean","COPY",FACE,{"derivedFrom":makeQuery(id+"F11.opExtrude","SWEPT_FACE",FACE,{"disambiguationData":[OSD([sQuery(id+"F10.wireOp",EDGE,"E10")])]})});
            var Q1;
            Q1=sQuery(id+"F0.wireOp",EDGE,"E0");
            circularPattern(context, id + "F12", {"faces" : qUnion([Q0]), "axis" : qUnion([Q1]), "angle" : 90 * degree, "instanceCount" : round(4), "patternType" : PatternType.FACE});
        }
        {
            var Q0;
            {var subQ0=makeQuery(id+"F2.opExtrude","CAP_FACE",FACE,{"disambiguationData":[OSD([sQuery(id+"F1.wireOp",EDGE,"E2"),sQuery(id+"F1.wireOp",EDGE,"E3"),sQuery(id+"F1.wireOp",EDGE,"E4"),sQuery(id+"F1.wireOp",EDGE,"E5"),sQuery(id+"F1.wireOp",EDGE,"E7")])],"isStart":false});Q0=makeQuery(id+"F5.opBoolean","MERGE",FACE,{"derivedFrom":[subQ0,makeQuery(id+"F4.opPattern","COPY",FACE,{"derivedFrom":subQ0,"instanceName":"1"}),makeQuery(id+"F4.opPattern","COPY",FACE,{"derivedFrom":subQ0,"instanceName":"2"}),makeQuery(id+"F4.opPattern","COPY",FACE,{"derivedFrom":subQ0,"instanceName":"3"}),makeQuery(id+"F4.opPattern","COPY",FACE,{"derivedFrom":subQ0,"instanceName":"4"}),makeQuery(id+"F4.opPattern","COPY",FACE,{"derivedFrom":subQ0,"instanceName":"5"}),makeQuery(id+"F4.opPattern","COPY",FACE,{"derivedFrom":subQ0,"instanceName":"6"}),makeQuery(id+"F4.opPattern","COPY",FACE,{"derivedFrom":subQ0,"instanceName":"7"}),makeQuery(id+"F4.opPattern","COPY",FACE,{"derivedFrom":subQ0,"instanceName":"8"}),makeQuery(id+"F4.opPattern","COPY",FACE,{"derivedFrom":subQ0,"instanceName":"9"}),makeQuery(id+"F4.opPattern","COPY",FACE,{"derivedFrom":subQ0,"instanceName":"10"}),makeQuery(id+"F4.opPattern","COPY",FACE,{"derivedFrom":subQ0,"instanceName":"11"}),makeQuery(id+"F4.opPattern","COPY",FACE,{"derivedFrom":subQ0,"instanceName":"12"}),makeQuery(id+"F4.opPattern","COPY",FACE,{"derivedFrom":subQ0,"instanceName":"13"}),makeQuery(id+"F4.opPattern","COPY",FACE,{"derivedFrom":subQ0,"instanceName":"14"}),makeQuery(id+"F4.opPattern","COPY",FACE,{"derivedFrom":subQ0,"instanceName":"15"}),makeQuery(id+"F4.opPattern","COPY",FACE,{"derivedFrom":subQ0,"instanceName":"16"}),makeQuery(id+"F4.opPattern","COPY",FACE,{"derivedFrom":subQ0,"instanceName":"17"}),makeQuery(id+"F4.opPattern","COPY",FACE,{"derivedFrom":subQ0,"instanceName":"18"}),makeQuery(id+"F4.opPattern","COPY",FACE,{"derivedFrom":subQ0,"instanceName":"19"}),makeQuery(id+"F4.opPattern","COPY",FACE,{"derivedFrom":subQ0,"instanceName":"20"}),makeQuery(id+"F4.opPattern","COPY",FACE,{"derivedFrom":subQ0,"instanceName":"21"}),makeQuery(id+"F4.opPattern","COPY",FACE,{"derivedFrom":subQ0,"instanceName":"22"}),makeQuery(id+"F4.opPattern","COPY",FACE,{"derivedFrom":subQ0,"instanceName":"23"}),makeQuery(id+"F4.opPattern","COPY",FACE,{"derivedFrom":subQ0,"instanceName":"24"}),makeQuery(id+"F4.opPattern","COPY",FACE,{"derivedFrom":subQ0,"instanceName":"25"}),makeQuery(id+"F4.opPattern","COPY",FACE,{"derivedFrom":subQ0,"instanceName":"26"}),makeQuery(id+"F4.opPattern","COPY",FACE,{"derivedFrom":subQ0,"instanceName":"27"}),makeQuery(id+"F4.opPattern","COPY",FACE,{"derivedFrom":subQ0,"instanceName":"28"}),makeQuery(id+"F4.opPattern","COPY",FACE,{"derivedFrom":subQ0,"instanceName":"29"}),makeQuery(id+"F4.opPattern","COPY",FACE,{"derivedFrom":subQ0,"instanceName":"30"}),makeQuery(id+"F4.opPattern","COPY",FACE,{"derivedFrom":subQ0,"instanceName":"31"}),makeQuery(id+"F4.opPattern","COPY",FACE,{"derivedFrom":subQ0,"instanceName":"32"}),makeQuery(id+"F4.opPattern","COPY",FACE,{"derivedFrom":subQ0,"instanceName":"33"}),makeQuery(id+"F4.opPattern","COPY",FACE,{"derivedFrom":subQ0,"instanceName":"34"}),makeQuery(id+"F4.opPattern","COPY",FACE,{"derivedFrom":subQ0,"instanceName":"35"}),makeQuery(id+"F4.opPattern","COPY",FACE,{"derivedFrom":subQ0,"instanceName":"36"}),makeQuery(id+"F4.opPattern","COPY",FACE,{"derivedFrom":subQ0,"instanceName":"37"}),makeQuery(id+"F4.opPattern","COPY",FACE,{"derivedFrom":subQ0,"instanceName":"38"}),makeQuery(id+"F4.opPattern","COPY",FACE,{"derivedFrom":subQ0,"instanceName":"39"}),makeQuery(id+"F4.opPattern","COPY",FACE,{"derivedFrom":subQ0,"instanceName":"40"}),makeQuery(id+"F4.opPattern","COPY",FACE,{"derivedFrom":subQ0,"instanceName":"41"}),makeQuery(id+"F4.opPattern","COPY",FACE,{"derivedFrom":subQ0,"instanceName":"42"}),makeQuery(id+"F4.opPattern","COPY",FACE,{"derivedFrom":subQ0,"instanceName":"43"}),makeQuery(id+"F4.opPattern","COPY",FACE,{"derivedFrom":subQ0,"instanceName":"44"}),makeQuery(id+"F4.opPattern","COPY",FACE,{"derivedFrom":subQ0,"instanceName":"45"}),makeQuery(id+"F4.opPattern","COPY",FACE,{"derivedFrom":subQ0,"instanceName":"46"}),makeQuery(id+"F4.opPattern","COPY",FACE,{"derivedFrom":subQ0,"instanceName":"47"}),makeQuery(id+"F4.opPattern","COPY",FACE,{"derivedFrom":subQ0,"instanceName":"48"}),makeQuery(id+"F4.opPattern","COPY",FACE,{"derivedFrom":subQ0,"instanceName":"49"}),makeQuery(id+"F4.opPattern","COPY",FACE,{"derivedFrom":subQ0,"instanceName":"50"}),makeQuery(id+"F4.opPattern","COPY",FACE,{"derivedFrom":subQ0,"instanceName":"51"}),makeQuery(id+"F4.opPattern","COPY",FACE,{"derivedFrom":subQ0,"instanceName":"52"}),makeQuery(id+"F4.opPattern","COPY",FACE,{"derivedFrom":subQ0,"instanceName":"53"}),makeQuery(id+"F4.opPattern","COPY",FACE,{"derivedFrom":subQ0,"instanceName":"54"}),makeQuery(id+"F4.opPattern","COPY",FACE,{"derivedFrom":subQ0,"instanceName":"55"}),makeQuery(id+"F4.opPattern","COPY",FACE,{"derivedFrom":subQ0,"instanceName":"56"}),makeQuery(id+"F4.opPattern","COPY",FACE,{"derivedFrom":subQ0,"instanceName":"57"}),makeQuery(id+"F4.opPattern","COPY",FACE,{"derivedFrom":subQ0,"instanceName":"58"}),makeQuery(id+"F4.opPattern","COPY",FACE,{"derivedFrom":subQ0,"instanceName":"59"}),makeQuery(id+"F4.opPattern","COPY",FACE,{"derivedFrom":subQ0,"instanceName":"60"}),makeQuery(id+"F4.opPattern","COPY",FACE,{"derivedFrom":subQ0,"instanceName":"61"}),makeQuery(id+"F4.opPattern","COPY",FACE,{"derivedFrom":subQ0,"instanceName":"62"}),makeQuery(id+"F4.opPattern","COPY",FACE,{"derivedFrom":subQ0,"instanceName":"63"}),makeQuery(id+"F4.opPattern","COPY",FACE,{"derivedFrom":subQ0,"instanceName":"64"}),makeQuery(id+"F4.opPattern","COPY",FACE,{"derivedFrom":subQ0,"instanceName":"65"}),makeQuery(id+"F4.opPattern","COPY",FACE,{"derivedFrom":subQ0,"instanceName":"66"}),makeQuery(id+"F4.opPattern","COPY",FACE,{"derivedFrom":subQ0,"instanceName":"67"}),makeQuery(id+"F4.opPattern","COPY",FACE,{"derivedFrom":subQ0,"instanceName":"68"}),makeQuery(id+"F4.opPattern","COPY",FACE,{"derivedFrom":subQ0,"instanceName":"69"}),makeQuery(id+"F4.opPattern","COPY",FACE,{"derivedFrom":subQ0,"instanceName":"70"}),makeQuery(id+"F4.opPattern","COPY",FACE,{"derivedFrom":subQ0,"instanceName":"71"})]});}
            var sketch = newSketch(context, id + "F13", { "sketchPlane" : qUnion([Q0])});
            skLineSegment(sketch, "E11", {"start": v(0, 0) * mm, "end": v(-66.78, 66.78) * mm, "construction": true});
            skCircle(sketch, "E12", {"center": v(-56.57, 56.57) * mm, "radius": 5 * mm});
            skSolve(sketch);
        }
        {
            var Q0;
            Q0=qSketchRegion(id+"F13",true);
            extrude(context, id + "F14", {"entities" : qUnion([Q0]), "operationType" : NewBodyOperationType.REMOVE, "endBound" : BoundingType.THROUGH_ALL, "oppositeDirection" : true, "depth" : 25 * mm});
        }
    });
